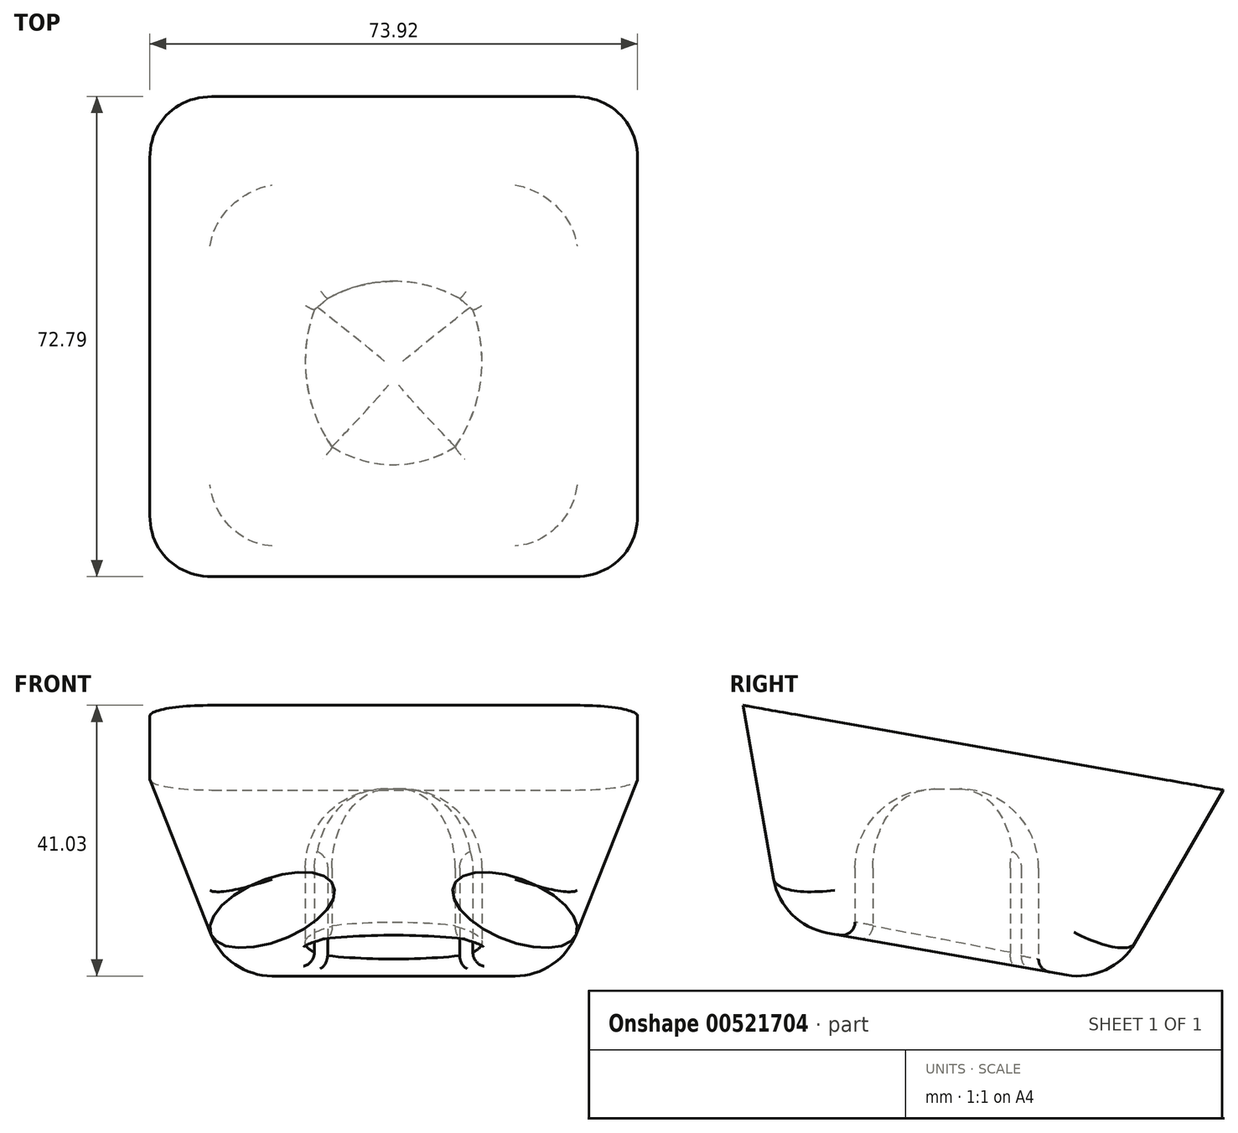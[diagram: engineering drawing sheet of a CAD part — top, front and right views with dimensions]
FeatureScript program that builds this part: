
annotation { "Feature Type Name" : "Feature", "Feature Type Description" : "" }
export const myFeature = defineFeature(function(context is Context, id is Id, definition is map)
    precondition{}
    {
        {
            var Q0;
            Q0=qCreatedBy(makeId("Top.planeOp"),FACE);
            var sketch = newSketch(context, id + "F0", { "sketchPlane" : qUnion([Q0])});
            skLineSegment(sketch, "E0.bottom", {"start": v(13.4, 13.9) * mm, "end": v(-13.4, 13.9) * mm, "construction": true});
            skLineSegment(sketch, "E0.top", {"start": v(13.4, -13.9) * mm, "end": v(-13.4, -13.9) * mm, "construction": true});
            skLineSegment(sketch, "E0.left", {"start": v(13.4, 13.9) * mm, "end": v(13.4, -13.9) * mm, "construction": true});
            skLineSegment(sketch, "E0.right", {"start": v(-13.4, 13.9) * mm, "end": v(-13.4, -13.9) * mm, "construction": true});
            skPoint(sketch, "E0.middle", {"position": v(0, 0) * mm});
            skLineSegment(sketch, "E1", {"start": v(0, 13.9) * mm, "end": v(0, -13.9) * mm, "construction": true});
            skArc(sketch, "E2", {"start": v(-9.35, -11.2) * mm, "mid": v(-4.87, -13.21) * mm, "end": v(0, -13.9) * mm});
            skLineSegment(sketch, "E3", {"start": v(0, 13.9) * mm, "end": v(0, 13.9) * mm});
            skArc(sketch, "E4", {"start": v(0, 13.9) * mm, "mid": v(-5.17, 13.23) * mm, "end": v(-10, 11.28) * mm});
            skLineSegment(sketch, "E5", {"start": v(-10, 11.28) * mm, "end": v(-12, 9.6) * mm});
            skArc(sketch, "E6", {"start": v(-12, 9.6) * mm, "mid": v(-13.22, -1.12) * mm, "end": v(-9.35, -11.2) * mm});
            skArc(sketch, "E7.MirrorCS", {"start": v(0, 13.9) * mm, "mid": v(5.17, 13.23) * mm, "end": v(10, 11.28) * mm});
            skLineSegment(sketch, "E8.MirrorCS", {"start": v(10, 11.28) * mm, "end": v(12, 9.6) * mm});
            skArc(sketch, "E9.MirrorCS", {"start": v(12, 9.6) * mm, "mid": v(13.22, -1.12) * mm, "end": v(9.35, -11.2) * mm});
            skArc(sketch, "E10.MirrorCS", {"start": v(9.35, -11.2) * mm, "mid": v(4.87, -13.21) * mm, "end": v(0, -13.9) * mm});
            skSolve(sketch);
        }
        {
            var Q0;
            Q0=makeQuery(id+"F0.imprint","IMPRINT",FACE,{"disambiguationData":[TD([[makeQuery(id+"F0.imprint","IMPRINT",EDGE,{"derivedFrom":sQuery(id+"F0.wireOp",EDGE,"E2")}),1.0]])]});
            extrude(context, id + "F1", {"entities" : qUnion([Q0]), "depth" : 25 * mm, "offsetDistance" : 25 * mm});
        }
        {
            var Q0;
            Q0=makeQuery(id+"F1.opExtrude","CAP_FACE",FACE,{"disambiguationData":[OSD([sQuery(id+"F0.wireOp",EDGE,"E2"),sQuery(id+"F0.wireOp",EDGE,"E4"),sQuery(id+"F0.wireOp",EDGE,"E5"),sQuery(id+"F0.wireOp",EDGE,"E6"),sQuery(id+"F0.wireOp",EDGE,"E7.MirrorCS"),sQuery(id+"F0.wireOp",EDGE,"E8.MirrorCS"),sQuery(id+"F0.wireOp",EDGE,"E9.MirrorCS"),sQuery(id+"F0.wireOp",EDGE,"E10.MirrorCS")])],"isStart":false});
            fillet(context, id + "F2", {"entities" : qUnion([Q0]), "radius" : 12 * mm, "tangentPropagation" : true, "allowEdgeOverflow" : false});
        }
        {
            var Q0;
            Q0=makeQuery(id+"F1.opExtrude","CAP_FACE",FACE,{"disambiguationData":[OSD([sQuery(id+"F0.wireOp",EDGE,"E2"),sQuery(id+"F0.wireOp",EDGE,"E4"),sQuery(id+"F0.wireOp",EDGE,"E5"),sQuery(id+"F0.wireOp",EDGE,"E6"),sQuery(id+"F0.wireOp",EDGE,"E7.MirrorCS"),sQuery(id+"F0.wireOp",EDGE,"E8.MirrorCS"),sQuery(id+"F0.wireOp",EDGE,"E9.MirrorCS"),sQuery(id+"F0.wireOp",EDGE,"E10.MirrorCS")])],"isStart":true});
            extrude(context, id + "F3", {"entities" : qUnion([Q0]), "operationType" : NewBodyOperationType.ADD, "depth" : 25 * mm, "offsetDistance" : 25 * mm});
        }
        {
            var Q0;
            Q0=qCreatedBy(makeId("Top.planeOp"),FACE);
            var sketch = newSketch(context, id + "F4", { "sketchPlane" : qUnion([Q0])});
            skLineSegment(sketch, "E11", {"start": v(0, 0) * mm, "end": v(97.7, 0) * mm, "construction": true});
            skSolve(sketch);
        }
        {
            var Q0;
            Q0=sQuery(id+"F4.wireOp",EDGE,"E11");
            var Q1;
            Q1=qCreatedBy(makeId("Top.planeOp"),FACE);
            cPlane(context, id + "F5", {"entities" : qUnion([Q0, Q1]), "cplaneType" : CPlaneType.LINE_ANGLE, "offset" : 25 * mm, "angle" : 10 * degree, "oppositeDirection" : true, "width" : 150 * mm, "height" : 150 * mm});
        }
        {
            var Q0;
            Q0=qCreatedBy(id+"F5.planeOp",FACE);
            var sketch = newSketch(context, id + "F6", { "sketchPlane" : qUnion([Q0])});
            skLineSegment(sketch, "E12.bottom", {"start": v(-25.4, 25.4) * mm, "end": v(25.4, 25.4) * mm});
            skLineSegment(sketch, "E12.top", {"start": v(-25.4, -25.4) * mm, "end": v(25.4, -25.4) * mm});
            skLineSegment(sketch, "E12.left", {"start": v(-25.4, 25.4) * mm, "end": v(-25.4, -25.4) * mm});
            skLineSegment(sketch, "E12.right", {"start": v(25.4, 25.4) * mm, "end": v(25.4, -25.4) * mm});
            skPoint(sketch, "E12.middle", {"position": v(0, 0) * mm});
            skSolve(sketch);
        }
        {
            var Q0;
            Q0=makeQuery(id+"F6.imprint","IMPRINT",FACE,{"disambiguationData":[TD([[makeQuery(id+"F6.imprint","IMPRINT",EDGE,{"derivedFrom":sQuery(id+"F6.wireOp",EDGE,"E12.bottom")}),-1.0]])]});
            extrude(context, id + "F7", {"entities" : qUnion([Q0]), "oppositeDirection" : true, "depth" : 31.75 * mm, "offsetDistance" : 25 * mm, "hasDraft" : true, "draftAngle" : 20 * degree});
        }
        {
            var Q0;
            Q0=makeQuery(id+"F1.opExtrude","SWEPT_BODY",BODY,{"disambiguationData":[OSD([sQuery(id+"F0.wireOp",EDGE,"E2"),sQuery(id+"F0.wireOp",EDGE,"E4"),sQuery(id+"F0.wireOp",EDGE,"E5"),sQuery(id+"F0.wireOp",EDGE,"E6"),sQuery(id+"F0.wireOp",EDGE,"E7.MirrorCS"),sQuery(id+"F0.wireOp",EDGE,"E8.MirrorCS"),sQuery(id+"F0.wireOp",EDGE,"E9.MirrorCS"),sQuery(id+"F0.wireOp",EDGE,"E10.MirrorCS")])]});
            var Q1;
            Q1=makeQuery(id+"F7.opExtrude","SWEPT_BODY",BODY,{"disambiguationData":[OSD([sQuery(id+"F6.wireOp",EDGE,"E12.bottom"),sQuery(id+"F6.wireOp",EDGE,"E12.top"),sQuery(id+"F6.wireOp",EDGE,"E12.left"),sQuery(id+"F6.wireOp",EDGE,"E12.right")])]});
            booleanBodies(context, id + "F8", {"operationType" : BooleanOperationType.SUBTRACTION, "tools" : qUnion([Q0]), "targets" : qUnion([Q1])});
        }
        {
            var Q0;
            Q0=makeQuery(id+"F7.opExtrude","SWEPT_EDGE",EDGE,{"disambiguationData":[OSD([sQuery(id+"F6.wireOp",EDGE,"E12.bottom"),sQuery(id+"F6.wireOp",EDGE,"E12.right")])]});
            var Q1;
            Q1=makeQuery(id+"F7.opExtrude","SWEPT_EDGE",EDGE,{"disambiguationData":[OSD([sQuery(id+"F6.wireOp",EDGE,"E12.top"),sQuery(id+"F6.wireOp",EDGE,"E12.right")])]});
            var Q2;
            Q2=makeQuery(id+"F7.opExtrude","SWEPT_EDGE",EDGE,{"disambiguationData":[OSD([sQuery(id+"F6.wireOp",EDGE,"E12.bottom"),sQuery(id+"F6.wireOp",EDGE,"E12.left")])]});
            var Q3;
            Q3=makeQuery(id+"F7.opExtrude","SWEPT_EDGE",EDGE,{"disambiguationData":[OSD([sQuery(id+"F6.wireOp",EDGE,"E12.top"),sQuery(id+"F6.wireOp",EDGE,"E12.left")])]});
            var Q4;
            Q4=makeQuery(id+"F7.opExtrude","CAP_EDGE",EDGE,{"disambiguationData":[OSD([sQuery(id+"F6.wireOp",EDGE,"E12.bottom")])],"isStart":true});
            var Q5;
            Q5=makeQuery(id+"F7.opExtrude","CAP_EDGE",EDGE,{"disambiguationData":[OSD([sQuery(id+"F6.wireOp",EDGE,"E12.right")])],"isStart":true});
            var Q6;
            Q6=makeQuery(id+"F7.opExtrude","CAP_EDGE",EDGE,{"disambiguationData":[OSD([sQuery(id+"F6.wireOp",EDGE,"E12.top")])],"isStart":true});
            var Q7;
            Q7=makeQuery(id+"F7.opExtrude","CAP_EDGE",EDGE,{"disambiguationData":[OSD([sQuery(id+"F6.wireOp",EDGE,"E12.left")])],"isStart":true});
            fillet(context, id + "F9", {"entities" : qUnion([Q0, Q1, Q2, Q3, Q4, Q5, Q6, Q7]), "radius" : 10 * mm, "tangentPropagation" : true, "allowEdgeOverflow" : false});
        }
        {
            var Q0;
            {var subQ0=sQuery(id+"F0.wireOp",EDGE,"E9.MirrorCS");Q0=makeQuery(id+"F8.opBoolean","INTERSECT",EDGE,{"derivedFrom":[makeQuery(id+"F3.boolean.opBoolean","MERGE",FACE,{"derivedFrom":[makeQuery(id+"F1.opExtrude","SWEPT_FACE",FACE,{"disambiguationData":[OSD([subQ0])]}),makeQuery(id+"F3.opExtrude","SWEPT_FACE",FACE,{"disambiguationData":[OSD([subQ0])]})]}),makeQuery(id+"F7.opExtrude","CAP_FACE",FACE,{"disambiguationData":[OSD([sQuery(id+"F6.wireOp",EDGE,"E12.bottom"),sQuery(id+"F6.wireOp",EDGE,"E12.top"),sQuery(id+"F6.wireOp",EDGE,"E12.left"),sQuery(id+"F6.wireOp",EDGE,"E12.right")])],"isStart":true})]});}
            var Q1;
            {var subQ0=sQuery(id+"F0.wireOp",EDGE,"E8.MirrorCS");Q1=makeQuery(id+"F8.opBoolean","INTERSECT",EDGE,{"derivedFrom":[makeQuery(id+"F3.boolean.opBoolean","MERGE",FACE,{"derivedFrom":[makeQuery(id+"F1.opExtrude","SWEPT_FACE",FACE,{"disambiguationData":[OSD([subQ0])]}),makeQuery(id+"F3.opExtrude","SWEPT_FACE",FACE,{"disambiguationData":[OSD([subQ0])]})]}),makeQuery(id+"F7.opExtrude","CAP_FACE",FACE,{"disambiguationData":[OSD([sQuery(id+"F6.wireOp",EDGE,"E12.bottom"),sQuery(id+"F6.wireOp",EDGE,"E12.top"),sQuery(id+"F6.wireOp",EDGE,"E12.left"),sQuery(id+"F6.wireOp",EDGE,"E12.right")])],"isStart":true})]});}
            var Q2;
            {var subQ0=sQuery(id+"F0.wireOp",EDGE,"E7.MirrorCS");var subQ1=sQuery(id+"F0.wireOp",EDGE,"E4");Q2=makeQuery(id+"F8.opBoolean","INTERSECT",EDGE,{"derivedFrom":[makeQuery(id+"F3.boolean.opBoolean","MERGE",FACE,{"derivedFrom":[makeQuery(id+"F1.opExtrude","SWEPT_FACE",FACE,{"disambiguationData":[OSD([subQ1,subQ0])]}),makeQuery(id+"F3.opExtrude","SWEPT_FACE",FACE,{"disambiguationData":[OSD([subQ1,subQ0])]})]}),makeQuery(id+"F7.opExtrude","CAP_FACE",FACE,{"disambiguationData":[OSD([sQuery(id+"F6.wireOp",EDGE,"E12.bottom"),sQuery(id+"F6.wireOp",EDGE,"E12.top"),sQuery(id+"F6.wireOp",EDGE,"E12.left"),sQuery(id+"F6.wireOp",EDGE,"E12.right")])],"isStart":true})]});}
            var Q3;
            {var subQ0=sQuery(id+"F0.wireOp",EDGE,"E5");Q3=makeQuery(id+"F8.opBoolean","INTERSECT",EDGE,{"derivedFrom":[makeQuery(id+"F3.boolean.opBoolean","MERGE",FACE,{"derivedFrom":[makeQuery(id+"F1.opExtrude","SWEPT_FACE",FACE,{"disambiguationData":[OSD([subQ0])]}),makeQuery(id+"F3.opExtrude","SWEPT_FACE",FACE,{"disambiguationData":[OSD([subQ0])]})]}),makeQuery(id+"F7.opExtrude","CAP_FACE",FACE,{"disambiguationData":[OSD([sQuery(id+"F6.wireOp",EDGE,"E12.bottom"),sQuery(id+"F6.wireOp",EDGE,"E12.top"),sQuery(id+"F6.wireOp",EDGE,"E12.left"),sQuery(id+"F6.wireOp",EDGE,"E12.right")])],"isStart":true})]});}
            var Q4;
            {var subQ0=sQuery(id+"F0.wireOp",EDGE,"E6");Q4=makeQuery(id+"F8.opBoolean","INTERSECT",EDGE,{"derivedFrom":[makeQuery(id+"F3.boolean.opBoolean","MERGE",FACE,{"derivedFrom":[makeQuery(id+"F1.opExtrude","SWEPT_FACE",FACE,{"disambiguationData":[OSD([subQ0])]}),makeQuery(id+"F3.opExtrude","SWEPT_FACE",FACE,{"disambiguationData":[OSD([subQ0])]})]}),makeQuery(id+"F7.opExtrude","CAP_FACE",FACE,{"disambiguationData":[OSD([sQuery(id+"F6.wireOp",EDGE,"E12.bottom"),sQuery(id+"F6.wireOp",EDGE,"E12.top"),sQuery(id+"F6.wireOp",EDGE,"E12.left"),sQuery(id+"F6.wireOp",EDGE,"E12.right")])],"isStart":true})]});}
            var Q5;
            {var subQ0=sQuery(id+"F0.wireOp",EDGE,"E10.MirrorCS");var subQ1=sQuery(id+"F0.wireOp",EDGE,"E2");Q5=makeQuery(id+"F8.opBoolean","INTERSECT",EDGE,{"derivedFrom":[makeQuery(id+"F3.boolean.opBoolean","MERGE",FACE,{"derivedFrom":[makeQuery(id+"F1.opExtrude","SWEPT_FACE",FACE,{"disambiguationData":[OSD([subQ1,subQ0])]}),makeQuery(id+"F3.opExtrude","SWEPT_FACE",FACE,{"disambiguationData":[OSD([subQ1,subQ0])]})]}),makeQuery(id+"F7.opExtrude","CAP_FACE",FACE,{"disambiguationData":[OSD([sQuery(id+"F6.wireOp",EDGE,"E12.bottom"),sQuery(id+"F6.wireOp",EDGE,"E12.top"),sQuery(id+"F6.wireOp",EDGE,"E12.left"),sQuery(id+"F6.wireOp",EDGE,"E12.right")])],"isStart":true})]});}
            fillet(context, id + "F10", {"entities" : qUnion([Q0, Q1, Q2, Q3, Q4, Q5]), "radius" : 2 * mm, "tangentPropagation" : true, "allowEdgeOverflow" : false});
        }
    });
